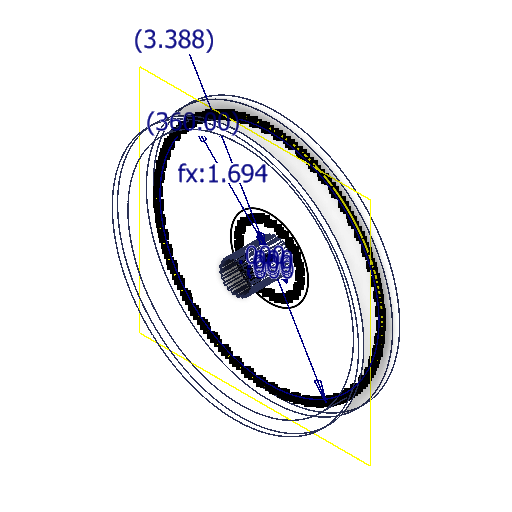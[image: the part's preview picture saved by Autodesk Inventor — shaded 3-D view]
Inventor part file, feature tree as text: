
AUTODESK INVENTOR PART (.ipt)
format: ipt  version: 2025.2 (Build 292293000, 293)  size: 623,104 bytes
history: native  units: in
note: dims shown in document units (in); Inventor stores cm internally (conversion verified against a paired STEP export)
features: sketch x6, extrude x4, plane x1
ambient origin geometry x8: Origin, YZ Plane, XZ Plane, XY Plane, X Axis, Y Axis, Z Axis, Center Point
bodies: Solid1 (feature_tree)
feature tree (11):
  extrude  "Extrusion1"  Depth=0.6181in TaperAngle=0.0deg
  plane  "Work Plane1"
  extrude  "Extrusion2"  Depth=3.388in
  extrude  "Extrusion3"  Depth=0.4331in
  extrude  "Extrusion5"  Depth=0.25in
  sketch  "Sketch8"  dims[d15=0.25in d16=0.8in d21=0.0in d22=0.0in d23=0.6181in d24=0.0in d39=3.7in d40=0.0in d41=0.0in d42=0.0in d43=0.0in d44=0.0in d45=0.0in d47=1.694in d48=3.388in d49=0.0in d50=0.0in d51=0.0in d52=22.8346in d54=360.0deg]
  sketch  "Sketch1"  dims[d0=3.7in d1=0.6181in d2=0.0in]
  sketch  "Sketch2"  dims[d3=-0.2953in d4=3.388in]
  sketch  "Sketch3"  dims[d8=0.0in d9=0.0in d13=0.25in]
  sketch  "Sketch5"  dims[d14=0.8in]
  sketch  "Sketch Circular Pattern2"  dims[d5=0.4331in d6=0.0in d7=0.4724in]
